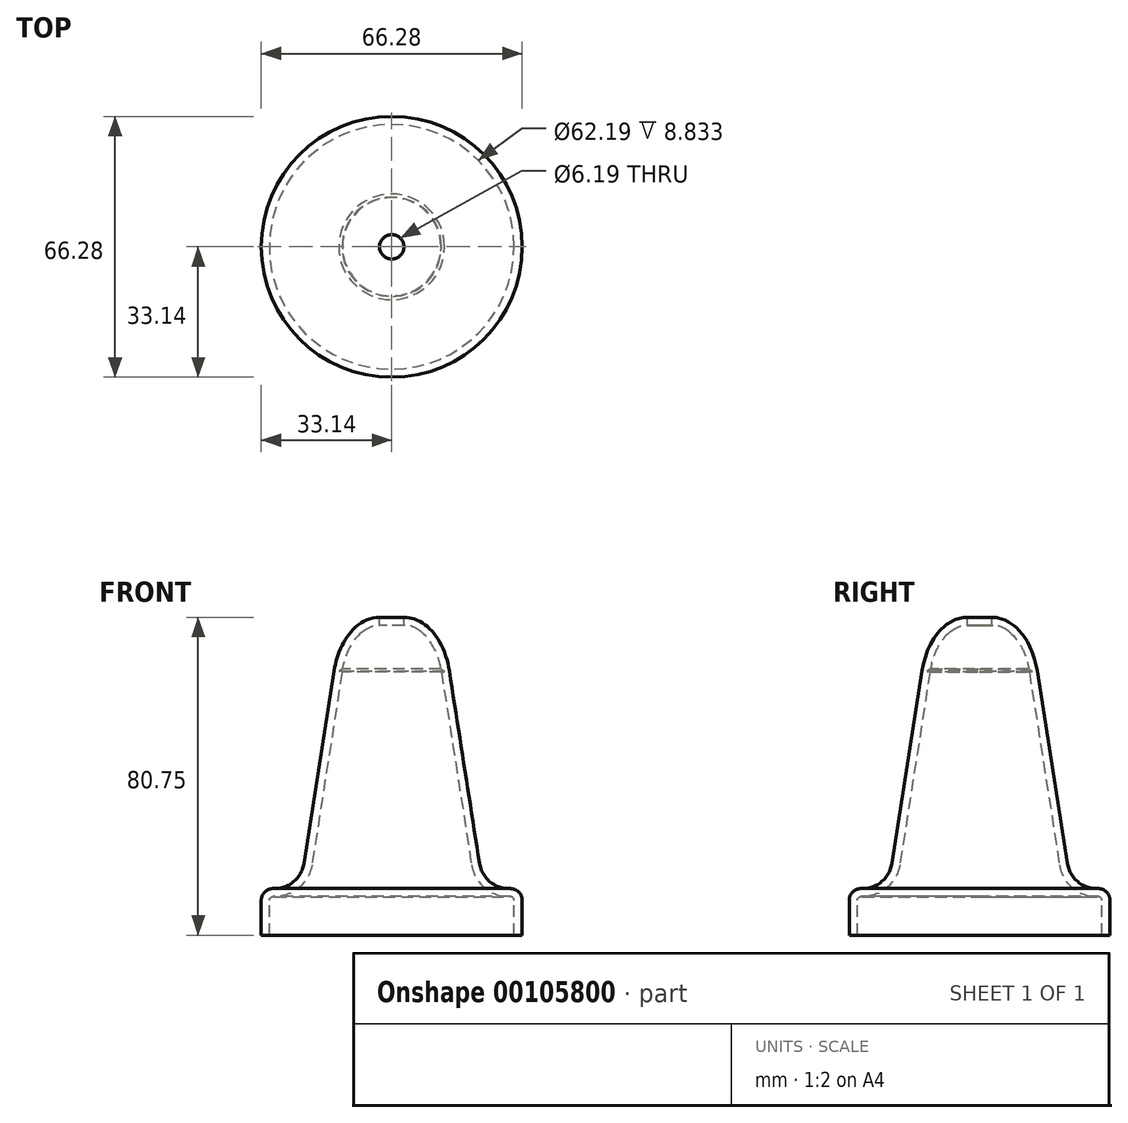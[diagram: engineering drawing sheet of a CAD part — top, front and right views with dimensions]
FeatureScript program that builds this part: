
annotation { "Feature Type Name" : "Feature", "Feature Type Description" : "" }
export const myFeature = defineFeature(function(context is Context, id is Id, definition is map)
    precondition{}
    {
        {
            var Q0;
            Q0=qCreatedBy(makeId("Right.planeOp"),FACE);
            var sketch = newSketch(context, id + "F0", { "sketchPlane" : qUnion([Q0])});
            skLineSegment(sketch, "E0", {"start": v(0, 52.86) * mm, "end": v(0, -48.48) * mm, "construction": true});
            skLineSegment(sketch, "E1", {"start": v(3.1, 52.86) * mm, "end": v(3.1, -48.74) * mm, "construction": true});
            skLineSegment(sketch, "E2", {"start": v(33.14, -27.9) * mm, "end": v(33.14, -19.06) * mm});
            skEllipticalArc(sketch, "E3", {});
            skLineSegment(sketch, "E4", {"start": v(14.63, 39.25) * mm, "end": v(22.3, -9.68) * mm});
            skArc(sketch, "E5", {"start": v(22.3, -9.68) * mm, "mid": v(24.95, -14.34) * mm, "end": v(30.03, -16.06) * mm});
            skPoint(sketch, "E6.visualSharp", {"position": v(33.14, -15.27) * mm});
            skArc(sketch, "E6.filletArc", {"start": v(33.14, -19.06) * mm, "mid": v(32.22, -16.9) * mm, "end": v(30.03, -16.06) * mm});
            skFitSpline(sketch, "E7.0", {"points": [v(12.62, 38.93) * mm, v(12.34, 40.7) * mm, v(11.63, 43.2) * mm, v(10.19, 46.03) * mm, v(8.93, 47.79) * mm, v(7.53, 49.17) * mm, v(6.06, 50.14) * mm, v(4.57, 50.7) * mm, v(3.59, 50.82) * mm, v(3.1, 50.82) * mm]});
            skLineSegment(sketch, "E7.1", {"start": v(31.1, -27.9) * mm, "end": v(31.1, -19.06) * mm});
            skArc(sketch, "E7.2", {"start": v(31.1, -19.06) * mm, "mid": v(30.8, -18.37) * mm, "end": v(30.1, -18.1) * mm});
            skArc(sketch, "E7.3", {"start": v(20.28, -10) * mm, "mid": v(23.65, -15.91) * mm, "end": v(30.1, -18.1) * mm});
            skLineSegment(sketch, "E7.4", {"start": v(12.62, 38.93) * mm, "end": v(20.28, -10) * mm});
            skLineSegment(sketch, "E8", {"start": v(31.1, -27.9) * mm, "end": v(33.14, -27.9) * mm});
            skLineSegment(sketch, "E9", {"start": v(3.1, 50.82) * mm, "end": v(3.1, 52.86) * mm});
            skLineSegment(sketch, "E10", {"start": v(12.62, 38.93) * mm, "end": v(14.63, 39.25) * mm});
            skLineSegment(sketch, "E11", {"start": v(9.83, 51.3) * mm, "end": v(6.4, 48.36) * mm});
            skLineSegment(sketch, "E12", {"start": v(11.12, 40.8) * mm, "end": v(13.9, 38.7) * mm});
            const initialGuessF0  = {"E3": [0.0030944710597395897, 0.03525747358798981, 0, 1, 0.01760641485452652, 0.011848910074809165, 4.941047712931551, 0]};
            skSetInitialGuess(sketch, initialGuessF0);
            skSolve(sketch);
        }
        {
            var Q0;
            {var subQ0=sQuery(id+"F0.wireOp",EDGE,"E9");Q0=makeQuery(id+"F0.imprint","IMPRINT",FACE,{"disambiguationData":[TD([[makeQuery(id+"F0.imprint","IMPRINT",EDGE,{"derivedFrom":subQ0}),-1.0]])]});}
            var Q1;
            {var subQ3=sQuery(id+"F0.wireOp",EDGE,"E12");var subQ5=sQuery(id+"F0.wireOp",EDGE,"E7.0");var subQ6=makeQuery(id+"F0.imprint","INTERSECT",VERTEX,{"derivedFrom":[subQ5,subQ3]});Q1=makeQuery(id+"F0.imprint","IMPRINT",FACE,{"disambiguationData":[TD([[makeQuery(id+"F0.imprint","IMPRINT",EDGE,{"disambiguationData":[TD([[subQ6,-1.0]])],"derivedFrom":subQ5}),-1.0]])]});}
            var Q2;
            Q2=makeQuery(id+"F0.imprint","IMPRINT",FACE,{"disambiguationData":[TD([[makeQuery(id+"F0.imprint","IMPRINT",EDGE,{"derivedFrom":sQuery(id+"F0.wireOp",EDGE,"E2")}),1.0]])]});
            var Q3;
            Q3=sQuery(id+"F0.wireOp",EDGE,"E0");
            revolve(context, id + "F1", {"entities" : qUnion([Q0, Q1, Q2]), "axis" : qUnion([Q3]), "revolveType" : RevolveType.FULL});
        }
    });
